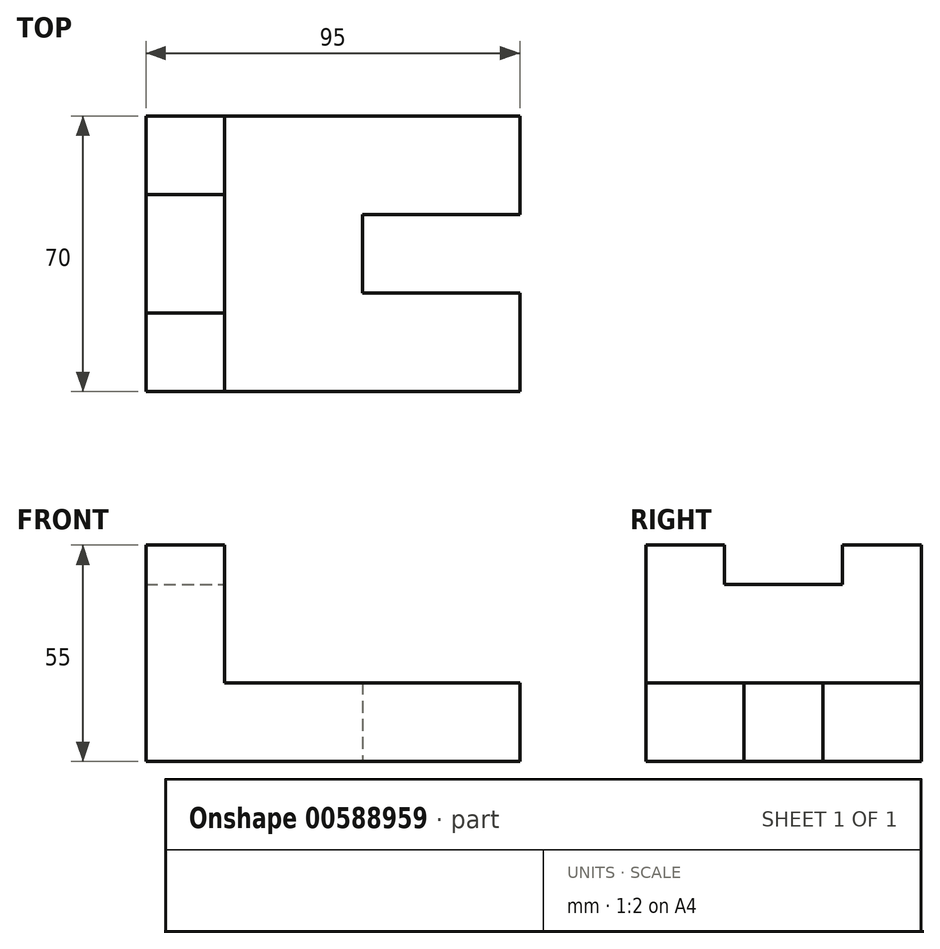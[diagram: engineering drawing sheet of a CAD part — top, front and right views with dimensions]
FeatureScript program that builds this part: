
annotation { "Feature Type Name" : "Feature", "Feature Type Description" : "" }
export const myFeature = defineFeature(function(context is Context, id is Id, definition is map)
    precondition{}
    {
        {
            var Q0;
            Q0=qCreatedBy(makeId("Top.planeOp"),FACE);
            var sketch = newSketch(context, id + "F0", { "sketchPlane" : qUnion([Q0])});
            skPoint(sketch, "E0.middle", {"position": v(0, 0) * mm});
            skLineSegment(sketch, "E1.bottom", {"start": v(47.5, -35) * mm, "end": v(-47.5, -35) * mm});
            skLineSegment(sketch, "E1.top", {"start": v(47.5, 35) * mm, "end": v(-47.5, 35) * mm});
            skLineSegment(sketch, "E1.left", {"start": v(47.5, -35) * mm, "end": v(47.5, -10) * mm});
            skLineSegment(sketch, "E1.right", {"start": v(-47.5, -35) * mm, "end": v(-47.5, 35) * mm});
            skLineSegment(sketch, "E2", {"start": v(7.5, 0) * mm, "end": v(7.5, 10) * mm});
            skLineSegment(sketch, "E3.MirrorCS", {"start": v(7.5, 0) * mm, "end": v(7.5, -10) * mm});
            skLineSegment(sketch, "E4", {"start": v(7.5, 10) * mm, "end": v(47.5, 10) * mm});
            skLineSegment(sketch, "E5", {"start": v(7.5, -10) * mm, "end": v(47.5, -10) * mm});
            skLineSegment(sketch, "E6.trimOffspring", {"start": v(47.5, 10) * mm, "end": v(47.5, 35) * mm});
            skSolve(sketch);
        }
        {
            var Q0;
            Q0=makeQuery(id+"F0.imprint","IMPRINT",FACE,{"disambiguationData":[TD([[makeQuery(id+"F0.imprint","IMPRINT",EDGE,{"derivedFrom":sQuery(id+"F0.wireOp",EDGE,"E1.bottom")}),-1.0]])]});
            extrude(context, id + "F1", {"entities" : qUnion([Q0]), "depth" : 20 * mm, "offsetDistance" : 25 * mm});
        }
        {
            var Q0;
            Q0=makeQuery(id+"F1.opExtrude","SWEPT_FACE",FACE,{"disambiguationData":[OSD([sQuery(id+"F0.wireOp",EDGE,"E1.bottom")])]});
            var sketch = newSketch(context, id + "F2", { "sketchPlane" : qUnion([Q0])});
            skLineSegment(sketch, "E7", {"start": v(-47.5, 20) * mm, "end": v(-47.5, 55) * mm});
            skLineSegment(sketch, "E8", {"start": v(-47.5, 55) * mm, "end": v(-27.5, 55) * mm});
            skLineSegment(sketch, "E9", {"start": v(-27.5, 55) * mm, "end": v(-27.5, 20) * mm});
            skLineSegment(sketch, "E10", {"start": v(-47.5, 20) * mm, "end": v(-27.5, 20) * mm});
            skSolve(sketch);
        }
        {
            var Q0;
            {var subQ0=sQuery(id+"F2.wireOp",EDGE,"E7");Q0=makeQuery(id+"F2.imprint","IMPRINT",FACE,{"disambiguationData":[TD([[makeQuery(id+"F2.imprint","IMPRINT",EDGE,{"derivedFrom":subQ0}),-1.0]])]});}
            extrude(context, id + "F3", {"entities" : qUnion([Q0]), "operationType" : NewBodyOperationType.ADD, "oppositeDirection" : true, "depth" : 70 * mm, "offsetDistance" : 25 * mm});
        }
        {
            var Q0;
            Q0=makeQuery(id+"F3.opExtrude","SWEPT_FACE",FACE,{"disambiguationData":[OSD([sQuery(id+"F2.wireOp",EDGE,"E9")])]});
            var sketch = newSketch(context, id + "F4", { "sketchPlane" : qUnion([Q0])});
            skLineSegment(sketch, "E11", {"start": v(-15, 55) * mm, "end": v(-15, 45) * mm});
            skLineSegment(sketch, "E12", {"start": v(-15, 45) * mm, "end": v(15, 45) * mm});
            skLineSegment(sketch, "E13", {"start": v(15, 45) * mm, "end": v(15, 55) * mm});
            skLineSegment(sketch, "E14", {"start": v(15, 55) * mm, "end": v(-15, 55) * mm});
            skSolve(sketch);
        }
        {
            var Q0;
            Q0=makeQuery(id+"F4.imprint","IMPRINT",FACE,{"disambiguationData":[TD([[makeQuery(id+"F4.imprint","IMPRINT",EDGE,{"derivedFrom":sQuery(id+"F4.wireOp",EDGE,"E11")}),1.0]])]});
            extrude(context, id + "F5", {"entities" : qUnion([Q0]), "operationType" : NewBodyOperationType.REMOVE, "endBound" : BoundingType.THROUGH_ALL, "oppositeDirection" : true, "depth" : 25 * mm, "offsetDistance" : 25 * mm});
        }
    });
